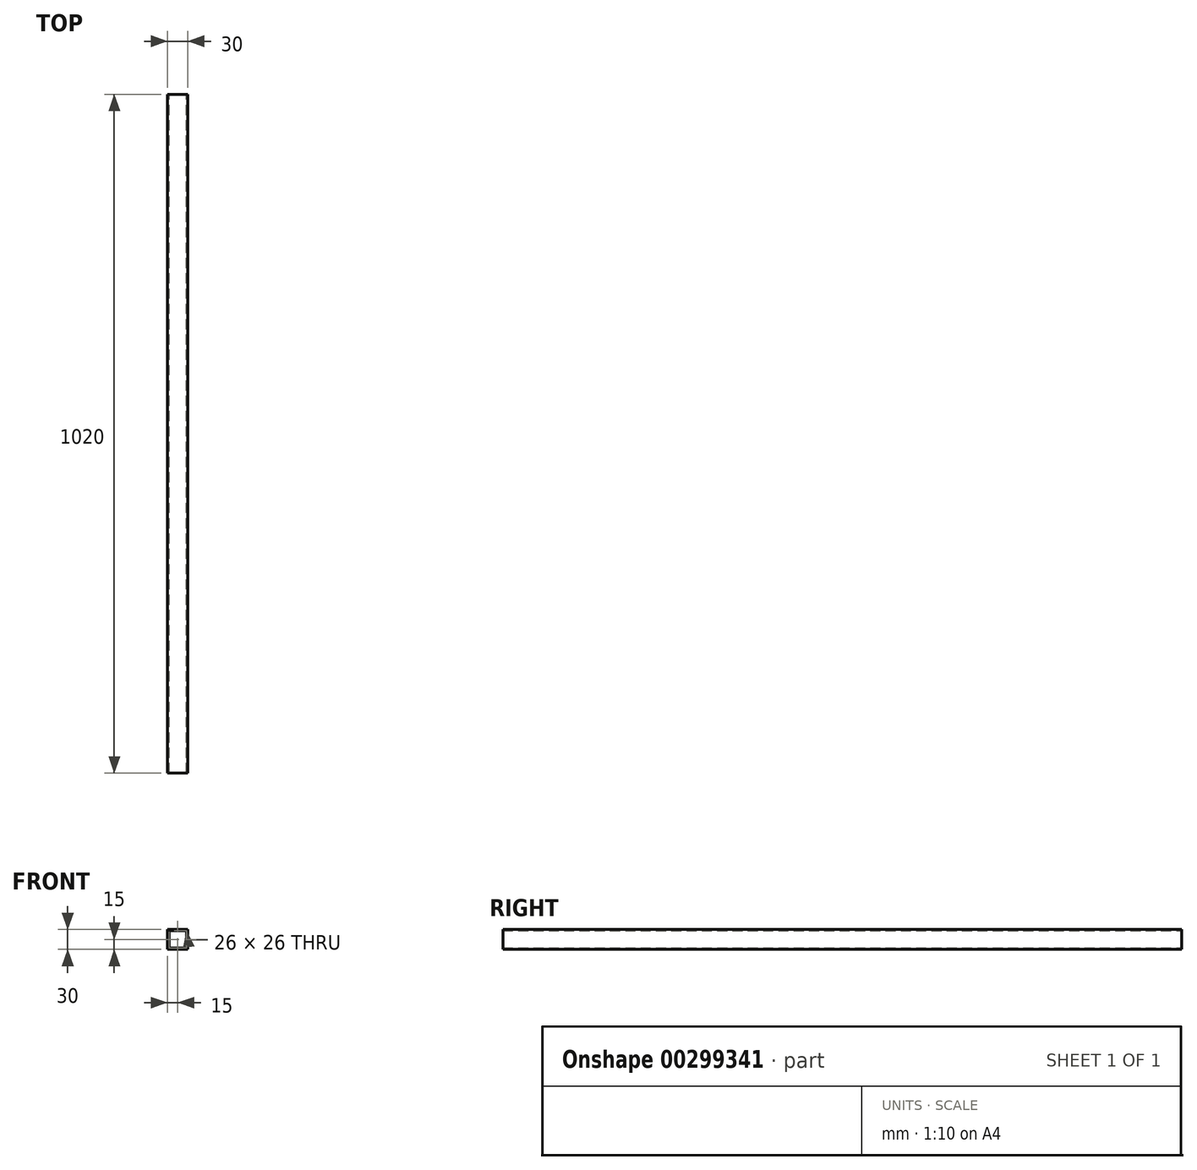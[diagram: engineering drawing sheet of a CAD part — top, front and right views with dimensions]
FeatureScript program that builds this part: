
annotation { "Feature Type Name" : "Feature", "Feature Type Description" : "" }
export const myFeature = defineFeature(function(context is Context, id is Id, definition is map)
    precondition{}
    {
        {
            var Q0;
            Q0=qCreatedBy(makeId("Front.planeOp"),FACE);
            var sketch = newSketch(context, id + "F0", { "sketchPlane" : qUnion([Q0])});
            skLineSegment(sketch, "E0.bottom", {"start": v(0, 0) * mm, "end": v(30, 0) * mm});
            skLineSegment(sketch, "E0.top", {"start": v(0, -30) * mm, "end": v(30, -30) * mm});
            skLineSegment(sketch, "E0.left", {"start": v(0, 0) * mm, "end": v(0, -30) * mm});
            skLineSegment(sketch, "E0.right", {"start": v(30, 0) * mm, "end": v(30, -30) * mm});
            skLineSegment(sketch, "E1.0", {"start": v(2, -2) * mm, "end": v(2, -28) * mm});
            skLineSegment(sketch, "E1.1", {"start": v(2, -2) * mm, "end": v(28, -2) * mm});
            skLineSegment(sketch, "E1.2", {"start": v(28, -2) * mm, "end": v(28, -28) * mm});
            skLineSegment(sketch, "E1.3", {"start": v(2, -28) * mm, "end": v(28, -28) * mm});
            skSolve(sketch);
        }
        {
            var Q0;
            Q0=makeQuery(id+"F0.imprint","IMPRINT",FACE,{"disambiguationData":[TD([[makeQuery(id+"F0.imprint","IMPRINT",EDGE,{"derivedFrom":sQuery(id+"F0.wireOp",EDGE,"E0.bottom")}),-1.0]])]});
            extrude(context, id + "F1", {"entities" : qUnion([Q0]), "depth" : 1020 * mm});
        }
    });
